# Revit family: KS ALU-PU 80 -s-, DS 50, M10-M12, Ø 42- 76,1
name_source: partatom
category: HLS-Bauteile
revit_build: Autodesk Revit 2017 (Build: 20190507_1515(x64)
units: mm (PartAtom-declared; Revit-internal decimal feet)

## family parameters
Arbeitsebenenbasiert = Ja
Beim Laden mit Abzugskörper schneiden = Nein
Bemaßung runder Anschluss = Durchmesser verwenden
Gemeinsam genutzt = Ja
Immer vertikal = Nein
Raumberechnungspunkt = Nein
Teiletyp = Normal

## types (8) — shared parameters
A = 75 mm
Anschluss = M10/M12
BP = 14 mm  [stored 0.0459318 ft]
Baustoffklasse = B2
DS = 50 mm  [stored 0.164042 ft]
DVS = 7 mm  [stored 0.0229659 ft]
Dichte Kern = 80 kg/m³
Dichte Mantel = 2.700 kg/m³
Dicke Mantel = 0,08 mm
Dämmkörper = ALU/PU
Dämmstärke = 50 mm  [stored 0.164042 ft]
Fabrikat = MEFA
Firma = MEFA Befestigungs- und Montagesysteme GmbH
HGA = 22 mm  [stored 0.0721785 ft]
Kurztext1 = Kälteschelle RG80s ALU/PU
L Ü Bogen = 19 mm  [stored 0.062336 ft]
MD = 3 mm  [stored 0.00984252 ft]
Material = Stahl
Material Mantel = Alufolie
Mengeneinheit = St
Oberflaeche = galvanisch verzinkt
Vorgabe-Ansicht = 1219 mm
Wasserdampfdiffusionswiderstand = 18750 µ
Wärmeleitfähigkeit = 0.025 W/mK
d1 = 7 mm  [stored 0.0229659 ft]
max. Temperaturbeständigkeit = 120 °C
mittl. Nenndruckfestigkeit Kern = 0,5 N/mm²
stat. Belastung Kern = 0,1 N/mm²
vpe = 1 St

## per-type parameters (varying)
- Kälteschelle ALU-PU 80 -s-, DS 50, M10/M12, Ø 42,4: AB=2 mm  [stored 0.00656168 ft]; Anschlußhöhe=74 mm; Artikelnummer=71704250; B=189 mm; Breite=192 mm; D=42 mm; D0=142 mm; DF1=20 mm  [stored 0.0656168 ft]; DF2=19 mm  [stored 0.062336 ft]; Dmax=44 mm  [stored 0.144357 ft]; Dmin=40 mm  [stored 0.131234 ft]; EAN=4250928441867; Gewicht=0.42 kg; Gewicht pro Bauteil=0.42 kg; H=170 mm; Kurztext2=42,4 mm Iso 50 x 40 mm M10/M12; L=40 mm  [stored 0.131234 ft]; MB=25 mm  [stored 0.082021 ft]; Materialname=DD11; R=71 mm; RM=74 mm  [stored 0.242782 ft]; Rohraußendurchmesser Kupfer=42 mm; Rohraußendurchmesser Stahl=42,4 mm; Rohrschellentyp=Omnia MB; S=169 mm; S1=161 mm; Schalenlänge=40 mm; max. zul. Last=0.20 kN
- Kälteschelle ALU-PU 80 -s-, DS 50, M10/M12, Ø 48,3: AB=2 mm  [stored 0.00656168 ft]; Anschlußhöhe=75 mm; Artikelnummer=71804850; B=196 mm; Breite=197 mm; D=48 mm; D0=148 mm; DF1=20 mm  [stored 0.0656168 ft]; DF2=20 mm  [stored 0.0656168 ft]; Dmax=50 mm  [stored 0.164042 ft]; Dmin=46 mm  [stored 0.150919 ft]; EAN=4250928441874; Gewicht=0.43 kg; Gewicht pro Bauteil=0.43 kg; H=176 mm; Kurztext2=48,3 mm Iso 50 x 50 mm M10/M12; L=50 mm  [stored 0.164042 ft]; MB=25 mm  [stored 0.082021 ft]; Materialname=DD11; R=74 mm  [stored 0.242782 ft]; RM=77 mm  [stored 0.252625 ft]; Rohraußendurchmesser Stahl=48,3 mm; Rohrschellentyp=Omnia MB; S=176 mm; S1=167 mm; Schalenlänge=50 mm; max. zul. Last=0.40 kN
- Kälteschelle ALU-PU 80 -s-, DS 50, M10/M12, Ø 54: AB=2 mm  [stored 0.00656168 ft]; Anschlußhöhe=75 mm; Artikelnummer=71805442; B=202 mm; Breite=234 mm; D=54 mm  [stored 0.177165 ft]; D0=154 mm; DF1=20 mm  [stored 0.0656168 ft]; DF2=20 mm  [stored 0.0656168 ft]; Dmax=56 mm  [stored 0.183727 ft]; Dmin=52 mm; EAN=4250928441881; Gewicht=0.58 kg; Gewicht pro Bauteil=0.58 kg; H=182 mm; Kurztext2=54 mm Iso 50 x 50 mm M10/M12; L=50 mm  [stored 0.164042 ft]; MB=30 mm  [stored 0.0984252 ft]; Materialname=S235; R=77 mm  [stored 0.252625 ft]; RM=80 mm  [stored 0.262467 ft]; Rohraußendurchmesser Stahl=54 mm; Rohrschellentyp=Maxima PSM; S=182 mm; S1=173 mm; Schalenlänge=50 mm; max. zul. Last=0.40 kN
- Kälteschelle ALU-PU 80 -s-, DS 50, M10/M12, Ø 57: AB=1 mm  [stored 0.00328084 ft]; Anschlußhöhe=75 mm; Artikelnummer=71805742; B=203 mm; Breite=220 mm; D=57 mm  [stored 0.187008 ft]; D0=157 mm; DF1=19 mm  [stored 0.062336 ft]; DF2=20 mm  [stored 0.0656168 ft]; Dmax=58 mm  [stored 0.190289 ft]; Dmin=56 mm  [stored 0.183727 ft]; EAN=4250928441898; Gewicht=0.58 kg; Gewicht pro Bauteil=0.58 kg; H=185 mm; Kurztext2=57 mm Iso 50 x 50 mm M10/M12; L=50 mm  [stored 0.164042 ft]; MB=30 mm  [stored 0.0984252 ft]; Materialname=S235; R=79 mm; RM=82 mm; Rohraußendurchmesser Stahl=57 mm; Rohrschellentyp=Maxima PSM; S=184 mm; S1=176 mm; Schalenlänge=50 mm; max. zul. Last=0.40 kN
- Kälteschelle ALU-PU 80 -s-, DS 50, M10/M12, Ø 60,3: AB=2 mm  [stored 0.00656168 ft]; Anschlußhöhe=74 mm; Artikelnummer=71806042; B=197 mm; Breite=223 mm; D=60 mm; D0=160 mm; DF1=19 mm  [stored 0.062336 ft]; DF2=20 mm  [stored 0.0656168 ft]; Dmax=52 mm; Dmin=58 mm  [stored 0.190289 ft]; EAN=4250928441904; Gewicht=0.58 kg; Gewicht pro Bauteil=0.58 kg; H=188 mm; Kurztext2=60,3 mm Iso 50 x 50 mm M10/M12; L=50 mm  [stored 0.164042 ft]; MB=30 mm  [stored 0.0984252 ft]; Materialname=S235; R=80 mm  [stored 0.262467 ft]; RM=83 mm; Rohraußendurchmesser Stahl=60,3 mm; Rohrschellentyp=Maxima PSM; S=178 mm; S1=179 mm; Schalenlänge=50 mm; max. zul. Last=0.40 kN
- Kälteschelle ALU-PU 80 -s-, DS 50, M10/M12, Ø 63,5: AB=2 mm  [stored 0.00656168 ft]; Anschlußhöhe=75 mm; Artikelnummer=71806442; B=208 mm; Breite=226 mm; D=64 mm; D0=164 mm; DF1=18 mm  [stored 0.0590551 ft]; DF2=19 mm  [stored 0.062336 ft]; Dmax=65 mm  [stored 0.213255 ft]; Dmin=62 mm  [stored 0.203412 ft]; EAN=4250928441911; Gewicht=0.60 kg; Gewicht pro Bauteil=0.60 kg; H=192 mm; Kurztext2=63,5 mm Iso 50 x 50 mm M10/M12; L=50 mm  [stored 0.164042 ft]; MB=30 mm  [stored 0.0984252 ft]; Materialname=S235; R=82 mm; RM=85 mm; Rohraußendurchmesser Stahl=63,5 mm; Rohrschellentyp=Maxima PSM; S=190 mm; S1=183 mm; Schalenlänge=50 mm; max. zul. Last=0.50 kN
- Kälteschelle ALU-PU 80 -s-, DS 50, M10/M12, Ø 70: AB=2 mm  [stored 0.00656168 ft]; Anschlußhöhe=75 mm; Artikelnummer=71907050; B=221 mm; Breite=219 mm; D=70 mm  [stored 0.229659 ft]; D0=170 mm; DF1=21 mm  [stored 0.0688976 ft]; DF2=22 mm  [stored 0.0721785 ft]; Dmax=72 mm  [stored 0.23622 ft]; Dmin=68 mm; EAN=4250928441928; Gewicht=0.53 kg; Gewicht pro Bauteil=0.53 kg; H=198 mm; Kurztext2=70 mm Iso 50 x 66 mm M10/M12; L=66 mm  [stored 0.216535 ft]; MB=25 mm  [stored 0.082021 ft]; Materialname=DD11; R=85 mm; RM=88 mm; Rohraußendurchmesser Stahl=70 mm; Rohrschellentyp=Omnia MB; S=200 mm; S1=189 mm; Schalenlänge=66 mm; max. zul. Last=0.60 kN
- Kälteschelle ALU-PU 80 -s-, DS 50, M10/M12, Ø 76,1: AB=2 mm  [stored 0.00656168 ft]; Anschlußhöhe=75 mm; Artikelnummer=71907650; B=224 mm; Breite=225 mm; D=76 mm; D0=176 mm; DF1=20 mm  [stored 0.0656168 ft]; DF2=20 mm  [stored 0.0656168 ft]; Dmax=78 mm  [stored 0.255906 ft]; Dmin=74 mm  [stored 0.242782 ft]; EAN=4250928441942; Gewicht=0.54 kg; Gewicht pro Bauteil=0.54 kg; H=204 mm; Kurztext2=76,1 mm Iso 50 x 66 mm M10/M12; L=66 mm  [stored 0.216535 ft]; MB=25 mm  [stored 0.082021 ft]; Materialname=DD11; R=88 mm; RM=91 mm; Rohraußendurchmesser Stahl=76,1 mm; Rohrschellentyp=Omnia MB; S=204 mm; S1=195 mm; Schalenlänge=66 mm; max. zul. Last=0.60 kN

note: [stored X ft] marks values corroborated as IEEE doubles in the binary element streams (Revit-internal decimal feet)

## geometry (parser evidence)
native form markers: Sweep x1
no freeform markers — native parametric forms only
